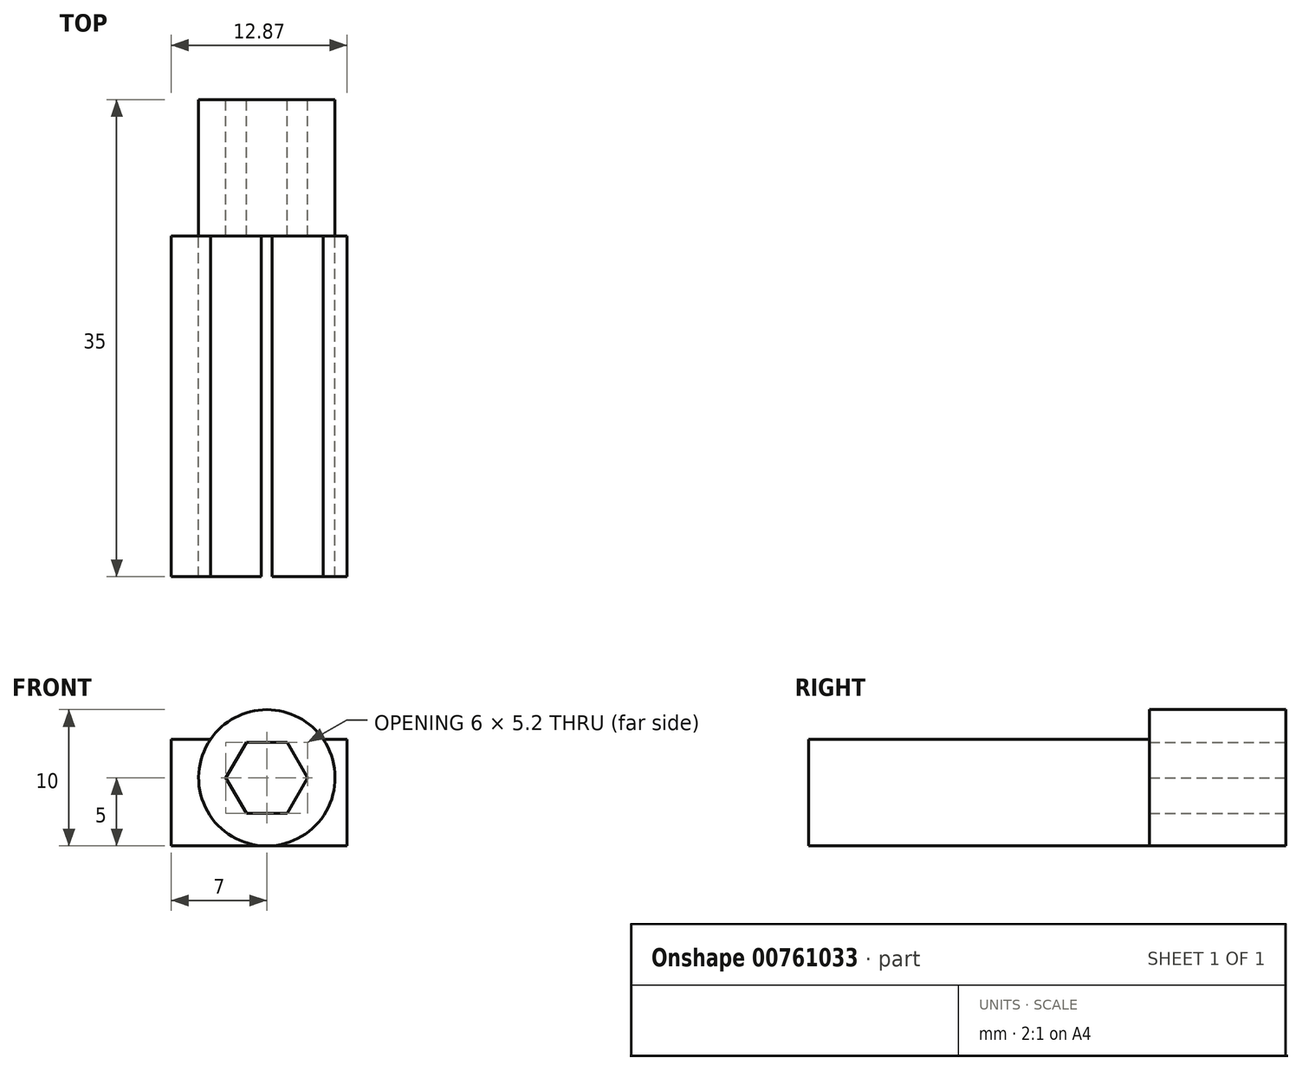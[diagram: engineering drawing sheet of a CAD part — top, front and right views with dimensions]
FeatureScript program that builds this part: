
annotation { "Feature Type Name" : "Feature", "Feature Type Description" : "" }
export const myFeature = defineFeature(function(context is Context, id is Id, definition is map)
    precondition{}
    {
        {
            var Q0;
            Q0=qCreatedBy(makeId("Front.planeOp"),FACE);
            var sketch = newSketch(context, id + "F0", { "sketchPlane" : qUnion([Q0])});
            skCircle(sketch, "E0.cCircle", {"center": v(0, 0) * mm, "radius": 2.6 * mm, "construction": true});
            skLineSegment(sketch, "E0.0", {"start": v(-1.5, 2.6) * mm, "end": v(1.5, 2.6) * mm});
            skLineSegment(sketch, "E0.1", {"start": v(1.5, 2.6) * mm, "end": v(3, 0) * mm});
            skLineSegment(sketch, "E0.2", {"start": v(3, 0) * mm, "end": v(1.5, -2.6) * mm});
            skLineSegment(sketch, "E0.3", {"start": v(1.5, -2.6) * mm, "end": v(-1.5, -2.6) * mm});
            skLineSegment(sketch, "E0.4", {"start": v(-1.5, -2.6) * mm, "end": v(-3, 0) * mm});
            skLineSegment(sketch, "E0.5", {"start": v(-3, 0) * mm, "end": v(-1.5, 2.6) * mm});
            skPoint(sketch, "E0.0.midPoint", {"position": v(0, 2.6) * mm});
            skCircle(sketch, "E1", {"center": v(0, 0) * mm, "radius": 5 * mm});
            skSolve(sketch);
        }
        {
            var Q0;
            Q0=makeQuery(id+"F0.imprint","IMPRINT",FACE,{"disambiguationData":[TD([[makeQuery(id+"F0.imprint","IMPRINT",EDGE,{"derivedFrom":sQuery(id+"F0.wireOp",EDGE,"E0.0")}),1.0]])]});
            extrude(context, id + "F1", {"entities" : qUnion([Q0]), "depth" : 10 * mm, "offsetDistance" : 25 * mm});
        }
        {
            var Q0;
            Q0=makeQuery(id+"F1.opExtrude","CAP_FACE",FACE,{"disambiguationData":[OSD([sQuery(id+"F0.wireOp",EDGE,"E0.0"),sQuery(id+"F0.wireOp",EDGE,"E0.1"),sQuery(id+"F0.wireOp",EDGE,"E0.2"),sQuery(id+"F0.wireOp",EDGE,"E0.3"),sQuery(id+"F0.wireOp",EDGE,"E0.4"),sQuery(id+"F0.wireOp",EDGE,"E0.5"),sQuery(id+"F0.wireOp",EDGE,"E1")])],"isStart":false});
            var sketch = newSketch(context, id + "F2", { "sketchPlane" : qUnion([Q0])});
            skLineSegment(sketch, "E2.bottom", {"start": v(-7, 2.8) * mm, "end": v(5.87, 2.8) * mm});
            skLineSegment(sketch, "E2.top", {"start": v(-7, -4.98) * mm, "end": v(5.87, -4.98) * mm});
            skLineSegment(sketch, "E2.left", {"start": v(-7, 2.8) * mm, "end": v(-7, -4.98) * mm});
            skLineSegment(sketch, "E2.right", {"start": v(5.87, 2.8) * mm, "end": v(5.87, -4.98) * mm});
            skSolve(sketch);
        }
        {
            var Q0;
            {var subQ0=sQuery(id+"F2.wireOp",EDGE,"E2.left");Q0=makeQuery(id+"F2.imprint","IMPRINT",FACE,{"disambiguationData":[TD([[makeQuery(id+"F2.imprint","IMPRINT",EDGE,{"derivedFrom":subQ0}),1.0]])]});}
            var Q1;
            {var subQ0=sQuery(id+"F2.wireOp",EDGE,"E2.right");Q1=makeQuery(id+"F2.imprint","IMPRINT",FACE,{"disambiguationData":[TD([[makeQuery(id+"F2.imprint","IMPRINT",EDGE,{"derivedFrom":subQ0}),-1.0]])]});}
            extrude(context, id + "F3", {"entities" : qUnion([Q0, Q1]), "depth" : 25 * mm, "offsetDistance" : 25 * mm});
        }
    });
